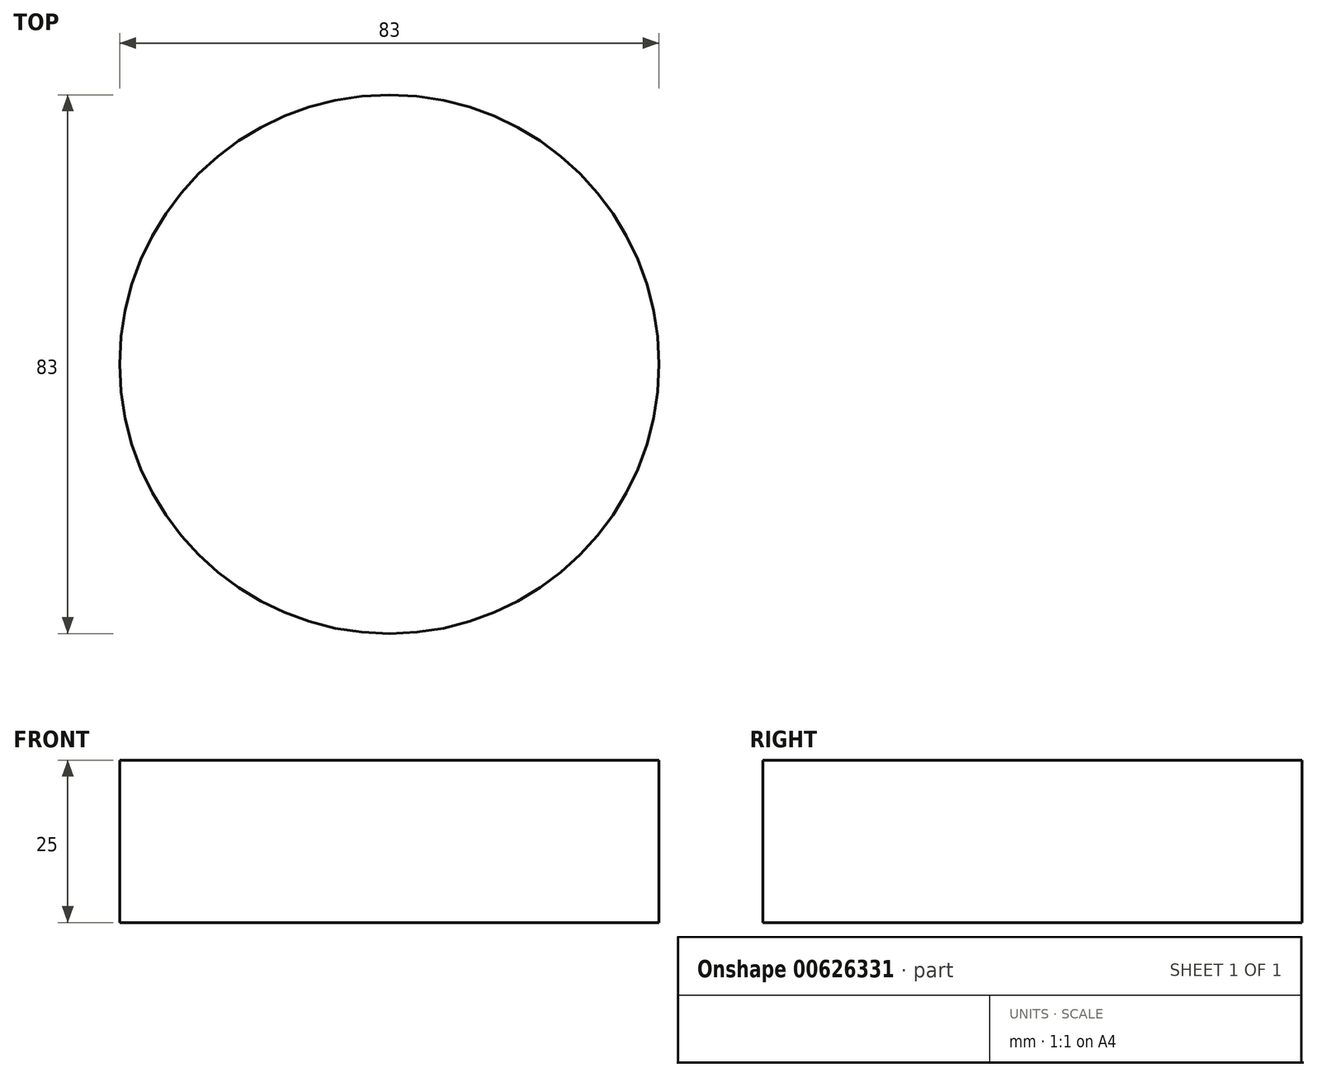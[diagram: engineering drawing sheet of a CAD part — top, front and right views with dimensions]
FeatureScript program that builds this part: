
annotation { "Feature Type Name" : "Feature", "Feature Type Description" : "" }
export const myFeature = defineFeature(function(context is Context, id is Id, definition is map)
    precondition{}
    {
        {
            var Q0;
            Q0=qCreatedBy(makeId("Top.planeOp"),FACE);
            var sketch = newSketch(context, id + "F0", { "sketchPlane" : qUnion([Q0])});
            skCircle(sketch, "E0", {"center": v(0, 0) * mm, "radius": 41.5 * mm});
            skSolve(sketch);
        }
        {
            var Q0;
            Q0 = qSketchRegion(id + "F0", true);
            extrude(context, id + "F1", {"entities" : qUnion([Q0]), "depth" : 25 * mm, "offsetDistance" : 25 * mm});
        }
    });
